# Revit family: DBLTD_TheSenatorGroup_OfficeChairs_AuraDining
name_source: partatom
category: Furniture
units: mm (PartAtom-declared; Revit-internal decimal feet)

## family parameters
Always vertical = Yes
Cut with Voids When Loaded = No
OmniClass Number = 23.40.20.00
OmniClass Title = General Furniture and Specialties
Render Appearance Source = Family Geometry
Room Calculation Point = No
Shared = Yes
Work Plane-Based = No

## types (8) — shared parameters
Assembly Code = E2020200
AssetType = Movable
Category = Pr_40_50_12_57 Office chairs
Color = Upholstery: Various.
Constituents = Seat and Back
DurationUnit = years
ExpectedLife = 5
Finish = Fully Upholstered
Keynote = Pr_40_50_12_57 Office chairs
Manufacturer = The Senator Group
ManufacturerName = The Senator Group
ManufacturerURL = https://www.allermuir.com
Material = Upholstered cut foam seat and back carcass. Plastic glides with felt.
Name = Chair
NominalHeight = 845 mm  [stored 2.77231 ft]
ProductInformation = https://www.allermuir.com
SeatingHeight = 465 mm  [stored 1.52559 ft]
Shape = Rectangular
URL = https://www.thesenatorgroup.com
Uniclass2015Code = Pr_40_50_12_57
Uniclass2015Title = Office chairs
Uniclass2015Version = Products v1.15
Version = 1
WarrantyDescription = The Senator Group warrants that its manufactured products are free from manufacturing defects - in materials or workmanship - for a period of five (5) years.
WarrantyDurationLabor = 5
WarrantyDurationParts = 5
WarrantyDurationUnit = years
WarrantyGuarantorLabor = https://www.thesenatorgroup.com
WarrantyGuarantorParts = https://www.thesenatorgroup.com
zero-valued in all types: Cost, Default Elevation

## per-type parameters (varying)
| type | ChairType | CornerUnit | EndUnit | Model | ModelNumber | NominalDepth | NominalWidth | SeatArray | SeatNumber | SeatSingle | Size |
| Straight Bench 2 Sections | Nested_DBLTD_TheSenatorGroup_OfficeChairs_AuraDining_Straight | No | No | AURDS11S | AURDS11S | 916 mm | 600 mm  [stored 1.9685 ft] | No | 2 | Yes | 845 (h) x 600 (w) x 916 (d) mm |
| Straight Bench 4 Sections | Nested_DBLTD_TheSenatorGroup_OfficeChairs_AuraDining_Straight | No | No | AURDS12S | AURDS12S | 916 mm | 1200 mm  [stored 3.93701 ft] | Yes | 2 | No | 845 (h) x 1200 (w) x 916 (d) mm |
| Straight Bench 6 Sections | Nested_DBLTD_TheSenatorGroup_OfficeChairs_AuraDining_Straight | No | No | AURDS13S | AURDS13S | 916 mm | 1800 mm  [stored 5.90551 ft] | Yes | 3 | No | 845 (h) x 1800 (w) x 916 (d) mm |
| Back to Back Bench 2 Sections | Nested_DBLTD_TheSenatorGroup_OfficeChairs_AuraDining_BacktoBack | No | No | AURDS11B | AURDS11B | 1550 mm  [stored 5.0853 ft] | 600 mm  [stored 1.9685 ft] | No | 2 | Yes | 845 (h) x 600 (w) x 1550 (d) mm |
| Back to Back Bench 4 Sections | Nested_DBLTD_TheSenatorGroup_OfficeChairs_AuraDining_BacktoBack | No | No | AURDS12B | AURDS12B | 1550 mm  [stored 5.0853 ft] | 1200 mm  [stored 3.93701 ft] | Yes | 2 | No | 845 (h) x 1200 (w) x 1550 (d) mm |
| Back to Back Bench 6 Sections | Nested_DBLTD_TheSenatorGroup_OfficeChairs_AuraDining_BacktoBack | No | No | AURDS13B | AURDS13B | 1550 mm  [stored 5.0853 ft] | 1800 mm  [stored 5.90551 ft] | Yes | 3 | No | 845 (h) x 1800 (w) x 1550 (d) mm |
| Back to Back End Piece | Nested_DBLTD_TheSenatorGroup_OfficeChairs_AuraDining_BacktoBack | No | Yes | AURDSE | AURDSE | 880 mm  [stored 2.88714 ft] | 1631 mm  [stored 5.35105 ft] | No | 2 | No | 845 (h) x 1631 (w) x 880 (d) mm |
| Straight Corner | Nested_DBLTD_TheSenatorGroup_OfficeChairs_AuraDining_BacktoBack | Yes | No | AURDSC | AURDSC | 1225 mm  [stored 4.01903 ft] | 1225 mm  [stored 4.01903 ft] | No | 2 | No | 845 (h) x 1225 (w) x 1225 (d) mm |

note: column(s) folded — value = type name in every type: Description, ModelReference, Type Comments

note: [stored X ft] marks values corroborated as IEEE doubles in the binary element streams (Revit-internal decimal feet)

## geometry (parser evidence)
native form markers: Sweep x13
no freeform markers — native parametric forms only
